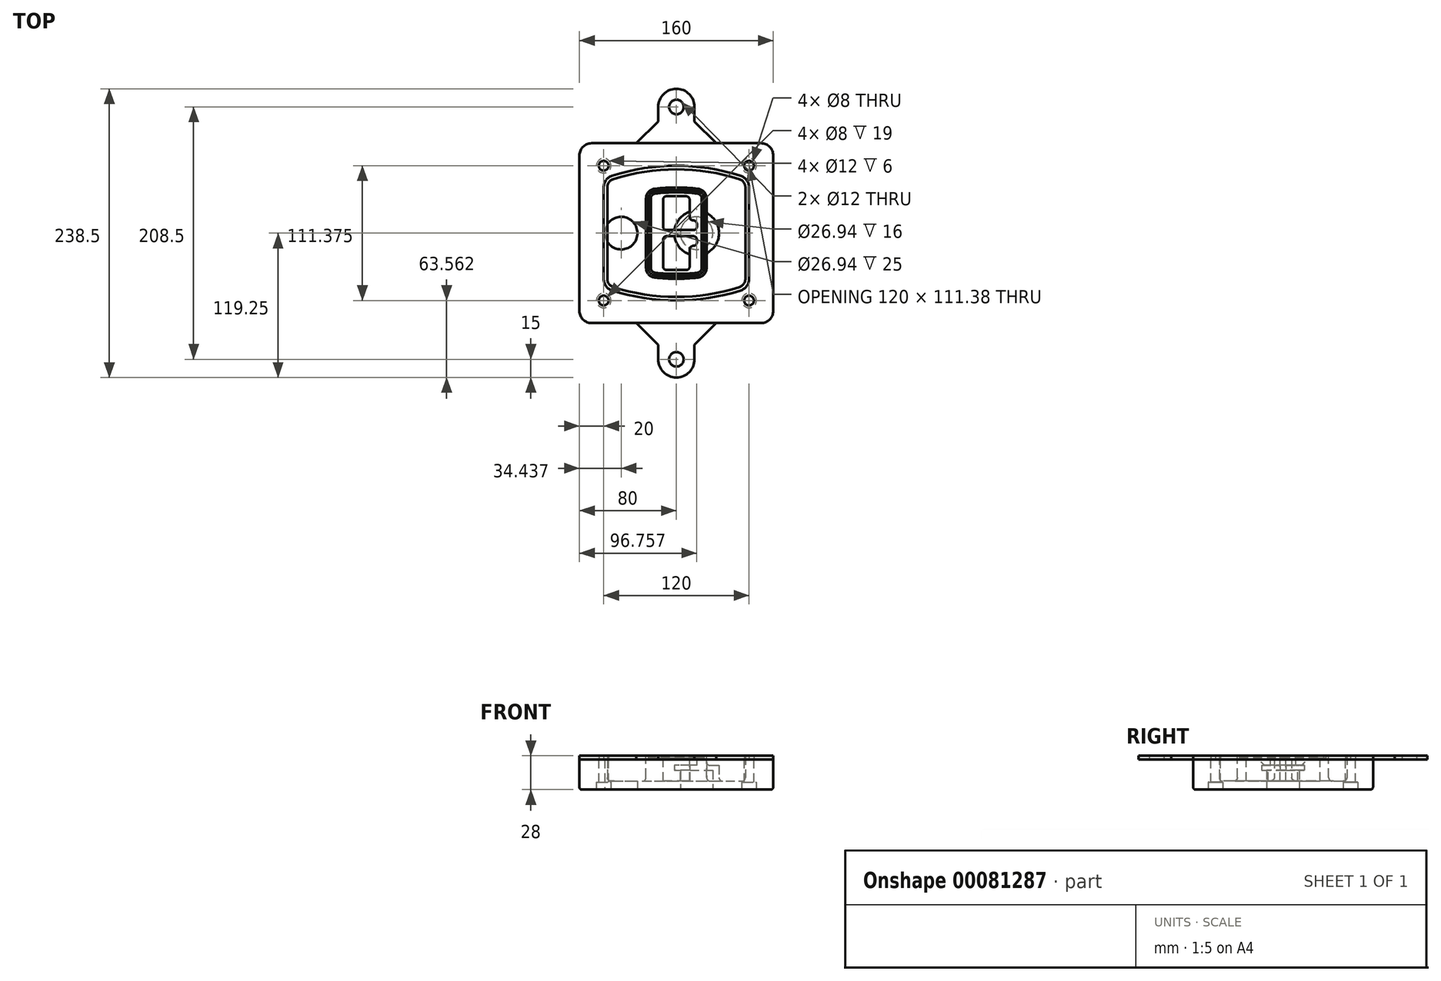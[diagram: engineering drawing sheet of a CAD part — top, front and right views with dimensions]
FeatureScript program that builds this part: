
annotation { "Feature Type Name" : "Feature", "Feature Type Description" : "" }
export const myFeature = defineFeature(function(context is Context, id is Id, definition is map)
    precondition{}
    {
        {
            var Q0;
            Q0=qCreatedBy(makeId("Top.planeOp"),FACE);
            var sketch = newSketch(context, id + "F0", { "sketchPlane" : qUnion([Q0])});
            skPoint(sketch, "E0.rect.middle", {"position": v(0, 0) * mm});
            skLineSegment(sketch, "E1.bottom", {"start": v(-70, -74.25) * mm, "end": v(70, -74.25) * mm});
            skLineSegment(sketch, "E1.top", {"start": v(-70, 74.25) * mm, "end": v(70, 74.25) * mm});
            skLineSegment(sketch, "E1.left", {"start": v(-80, -64.25) * mm, "end": v(-80, 64.25) * mm});
            skLineSegment(sketch, "E1.right", {"start": v(80, -64.25) * mm, "end": v(80, 64.25) * mm});
            skLineSegment(sketch, "E2", {"start": v(-80, 74.25) * mm, "end": v(80, -74.25) * mm, "construction": true});
            skLineSegment(sketch, "E3", {"start": v(80, 74.25) * mm, "end": v(-80, -74.25) * mm, "construction": true});
            skCircle(sketch, "E4", {"center": v(-60, 55.69) * mm, "radius": 4 * mm});
            skCircle(sketch, "E5", {"center": v(60, 55.69) * mm, "radius": 4 * mm});
            skCircle(sketch, "E6", {"center": v(60, -55.69) * mm, "radius": 4 * mm});
            skCircle(sketch, "E7", {"center": v(-60, -55.69) * mm, "radius": 4 * mm});
            skLineSegment(sketch, "E8", {"start": v(-60, 55.69) * mm, "end": v(60, 55.69) * mm, "construction": true});
            skLineSegment(sketch, "E9", {"start": v(60, 55.69) * mm, "end": v(60, -55.69) * mm, "construction": true});
            skLineSegment(sketch, "E10", {"start": v(60, -55.69) * mm, "end": v(-60, -55.69) * mm, "construction": true});
            skLineSegment(sketch, "E11", {"start": v(-60, -55.69) * mm, "end": v(-60, 55.69) * mm, "construction": true});
            skLineSegment(sketch, "E12", {"start": v(-60, 37.87) * mm, "end": v(-60, -37.87) * mm});
            skLineSegment(sketch, "E13", {"start": v(60, 37.87) * mm, "end": v(60, -37.87) * mm});
            skArc(sketch, "E14", {"start": v(53.05, 47.4) * mm, "mid": v(0, 55.69) * mm, "end": v(-53.05, 47.4) * mm});
            skArc(sketch, "E15", {"start": v(-53.05, -47.4) * mm, "mid": v(0, -55.69) * mm, "end": v(53.05, -47.4) * mm});
            skLineSegment(sketch, "E16", {"start": v(-60, 0) * mm, "end": v(60, 0) * mm, "construction": true});
            skPoint(sketch, "E17.visualSharp", {"position": v(-60, -45) * mm});
            skArc(sketch, "E17.filletArc", {"start": v(-60, -37.87) * mm, "mid": v(-58.08, -43.76) * mm, "end": v(-53.05, -47.4) * mm});
            skPoint(sketch, "E18.visualSharp", {"position": v(-60, 45) * mm});
            skArc(sketch, "E18.filletArc", {"start": v(-53.05, 47.4) * mm, "mid": v(-58.08, 43.76) * mm, "end": v(-60, 37.87) * mm});
            skPoint(sketch, "E19.visualSharp", {"position": v(60, 45) * mm});
            skArc(sketch, "E19.filletArc", {"start": v(60, 37.87) * mm, "mid": v(58.08, 43.76) * mm, "end": v(53.05, 47.4) * mm});
            skPoint(sketch, "E20.visualSharp", {"position": v(60, -45) * mm});
            skArc(sketch, "E20.filletArc", {"start": v(53.05, -47.4) * mm, "mid": v(58.08, -43.76) * mm, "end": v(60, -37.87) * mm});
            skPoint(sketch, "E21.visualSharp", {"position": v(-80, 74.25) * mm});
            skArc(sketch, "E21.filletArc", {"start": v(-70, 74.25) * mm, "mid": v(-77.07, 71.32) * mm, "end": v(-80, 64.25) * mm});
            skPoint(sketch, "E22.visualSharp", {"position": v(80, 74.25) * mm});
            skArc(sketch, "E22.filletArc", {"start": v(80, 64.25) * mm, "mid": v(77.07, 71.32) * mm, "end": v(70, 74.25) * mm});
            skPoint(sketch, "E23.visualSharp", {"position": v(80, -74.25) * mm});
            skArc(sketch, "E23.filletArc", {"start": v(70, -74.25) * mm, "mid": v(77.07, -71.32) * mm, "end": v(80, -64.25) * mm});
            skPoint(sketch, "E24.visualSharp", {"position": v(-80, -74.25) * mm});
            skArc(sketch, "E24.filletArc", {"start": v(-80, -64.25) * mm, "mid": v(-77.07, -71.32) * mm, "end": v(-70, -74.25) * mm});
            skArc(sketch, "E25.0", {"start": v(57, 37.87) * mm, "mid": v(55.66, 42) * mm, "end": v(52.14, 44.53) * mm});
            skLineSegment(sketch, "E25.1", {"start": v(57, 37.87) * mm, "end": v(57, -37.87) * mm});
            skArc(sketch, "E25.2", {"start": v(52.14, -44.53) * mm, "mid": v(55.66, -42) * mm, "end": v(57, -37.87) * mm});
            skArc(sketch, "E25.3", {"start": v(-52.14, -44.53) * mm, "mid": v(0, -52.69) * mm, "end": v(52.14, -44.53) * mm});
            skArc(sketch, "E25.4", {"start": v(-57, -37.87) * mm, "mid": v(-55.66, -42) * mm, "end": v(-52.14, -44.53) * mm});
            skArc(sketch, "E25.5", {"start": v(52.14, 44.53) * mm, "mid": v(0, 52.69) * mm, "end": v(-52.14, 44.53) * mm});
            skLineSegment(sketch, "E25.6", {"start": v(-57, 37.87) * mm, "end": v(-57, -37.87) * mm});
            skArc(sketch, "E25.7", {"start": v(-52.14, 44.53) * mm, "mid": v(-55.66, 42) * mm, "end": v(-57, 37.87) * mm});
            skArc(sketch, "E26.0", {"start": v(-54.27, 51.2) * mm, "mid": v(-61.31, 46.12) * mm, "end": v(-64, 37.87) * mm});
            skArc(sketch, "E26.1", {"start": v(54.27, 51.2) * mm, "mid": v(0, 59.69) * mm, "end": v(-54.27, 51.2) * mm});
            skArc(sketch, "E26.2", {"start": v(64, 37.87) * mm, "mid": v(61.31, 46.12) * mm, "end": v(54.27, 51.2) * mm});
            skLineSegment(sketch, "E26.3", {"start": v(64, 37.87) * mm, "end": v(64, -37.87) * mm});
            skArc(sketch, "E26.4", {"start": v(54.27, -51.2) * mm, "mid": v(61.31, -46.12) * mm, "end": v(64, -37.87) * mm});
            skLineSegment(sketch, "E26.5", {"start": v(-64, 37.87) * mm, "end": v(-64, -37.87) * mm});
            skArc(sketch, "E26.6", {"start": v(-54.27, -51.2) * mm, "mid": v(0, -59.69) * mm, "end": v(54.27, -51.2) * mm});
            skArc(sketch, "E26.7", {"start": v(-64, -37.87) * mm, "mid": v(-61.31, -46.12) * mm, "end": v(-54.27, -51.2) * mm});
            skSolve(sketch);
        }
        {
            var Q0;
            Q0=makeQuery(id+"F0.imprint","IMPRINT",FACE,{"disambiguationData":[TD([[makeQuery(id+"F0.imprint","IMPRINT",EDGE,{"derivedFrom":sQuery(id+"F0.wireOp",EDGE,"E1.bottom")}),1.0]])]});
            var Q1;
            Q1=makeQuery(id+"F0.imprint","IMPRINT",FACE,{"disambiguationData":[TD([[makeQuery(id+"F0.imprint","IMPRINT",EDGE,{"derivedFrom":sQuery(id+"F0.wireOp",EDGE,"E12")}),1.0]])]});
            var Q2;
            Q2=makeQuery(id+"F0.imprint","IMPRINT",FACE,{"disambiguationData":[TD([[makeQuery(id+"F0.imprint","IMPRINT",EDGE,{"derivedFrom":sQuery(id+"F0.wireOp",EDGE,"E25.0")}),1.0]])]});
            var Q3;
            Q3=makeQuery(id+"F0.imprint","IMPRINT",FACE,{"disambiguationData":[TD([[makeQuery(id+"F0.imprint","IMPRINT",EDGE,{"derivedFrom":sQuery(id+"F0.wireOp",EDGE,"E12")}),-1.0]])]});
            extrude(context, id + "F1", {"entities" : qUnion([Q0, Q1, Q2, Q3]), "oppositeDirection" : true, "depth" : 25 * mm});
        }
        {
            var Q0;
            Q0=makeQuery(id+"F0.imprint","IMPRINT",FACE,{"disambiguationData":[TD([[makeQuery(id+"F0.imprint","IMPRINT",EDGE,{"derivedFrom":sQuery(id+"F0.wireOp",EDGE,"E12")}),1.0]])]});
            extrude(context, id + "F2", {"entities" : qUnion([Q0]), "operationType" : NewBodyOperationType.ADD, "depth" : 3 * mm});
        }
        {
            var Q0;
            Q0=makeQuery(id+"F0.imprint","IMPRINT",FACE,{"disambiguationData":[TD([[makeQuery(id+"F0.imprint","IMPRINT",EDGE,{"derivedFrom":sQuery(id+"F0.wireOp",EDGE,"E25.0")}),1.0]])]});
            extrude(context, id + "F3", {"entities" : qUnion([Q0]), "operationType" : NewBodyOperationType.REMOVE, "oppositeDirection" : true, "depth" : 18 * mm});
        }
        {
            var Q0;
            Q0=makeQuery(id+"F2.opExtrude","CAP_FACE",FACE,{"disambiguationData":[OSD([sQuery(id+"F0.wireOp",EDGE,"E12"),sQuery(id+"F0.wireOp",EDGE,"E13"),sQuery(id+"F0.wireOp",EDGE,"E14"),sQuery(id+"F0.wireOp",EDGE,"E15"),sQuery(id+"F0.wireOp",EDGE,"E17.filletArc"),sQuery(id+"F0.wireOp",EDGE,"E18.filletArc"),sQuery(id+"F0.wireOp",EDGE,"E19.filletArc"),sQuery(id+"F0.wireOp",EDGE,"E20.filletArc"),sQuery(id+"F0.wireOp",EDGE,"E25.0"),sQuery(id+"F0.wireOp",EDGE,"E25.1"),sQuery(id+"F0.wireOp",EDGE,"E25.2"),sQuery(id+"F0.wireOp",EDGE,"E25.3"),sQuery(id+"F0.wireOp",EDGE,"E25.4"),sQuery(id+"F0.wireOp",EDGE,"E25.5"),sQuery(id+"F0.wireOp",EDGE,"E25.6"),sQuery(id+"F0.wireOp",EDGE,"E25.7")])],"isStart":false});
            var sketch = newSketch(context, id + "F4", { "sketchPlane" : qUnion([Q0])});
            skArc(sketch, "E27.0", {"start": v(-17.92, -36.65) * mm, "mid": v(0, -37.69) * mm, "end": v(17.92, -36.65) * mm});
            skArc(sketch, "E28.0", {"start": v(17.92, 36.65) * mm, "mid": v(0, 37.69) * mm, "end": v(-17.92, 36.65) * mm});
            skLineSegment(sketch, "E29", {"start": v(-25, 28.7) * mm, "end": v(-25, -28.7) * mm});
            skLineSegment(sketch, "E30", {"start": v(25, 28.7) * mm, "end": v(25, -28.7) * mm});
            skLineSegment(sketch, "E31", {"start": v(-25, 35.67) * mm, "end": v(25, 35.67) * mm, "construction": true});
            skLineSegment(sketch, "E32", {"start": v(-25, -35.67) * mm, "end": v(25, -35.67) * mm, "construction": true});
            skPoint(sketch, "E33.visualSharp", {"position": v(-25, 35.67) * mm});
            skArc(sketch, "E33.filletArc", {"start": v(-17.92, 36.65) * mm, "mid": v(-22.97, 34.03) * mm, "end": v(-25, 28.7) * mm});
            skPoint(sketch, "E34.visualSharp", {"position": v(25, 35.67) * mm});
            skArc(sketch, "E34.filletArc", {"start": v(25, 28.7) * mm, "mid": v(22.97, 34.03) * mm, "end": v(17.92, 36.65) * mm});
            skPoint(sketch, "E35.visualSharp", {"position": v(25, -35.67) * mm});
            skArc(sketch, "E35.filletArc", {"start": v(17.92, -36.65) * mm, "mid": v(22.97, -34.03) * mm, "end": v(25, -28.7) * mm});
            skPoint(sketch, "E36.visualSharp", {"position": v(-25, -35.67) * mm});
            skArc(sketch, "E36.filletArc", {"start": v(-25, -28.7) * mm, "mid": v(-22.97, -34.03) * mm, "end": v(-17.92, -36.65) * mm});
            skArc(sketch, "E37.0", {"start": v(52.14, 44.53) * mm, "mid": v(0, 52.69) * mm, "end": v(-52.14, 44.53) * mm});
            skArc(sketch, "E37.1", {"start": v(-52.14, 44.53) * mm, "mid": v(-55.66, 42) * mm, "end": v(-57, 37.87) * mm});
            skLineSegment(sketch, "E37.2", {"start": v(-57, 37.87) * mm, "end": v(-57, -37.87) * mm});
            skArc(sketch, "E37.3", {"start": v(-57, -37.87) * mm, "mid": v(-55.66, -42) * mm, "end": v(-52.14, -44.53) * mm});
            skArc(sketch, "E37.4", {"start": v(-52.14, -44.53) * mm, "mid": v(0, -52.69) * mm, "end": v(52.14, -44.53) * mm});
            skArc(sketch, "E37.5", {"start": v(52.14, -44.53) * mm, "mid": v(55.66, -42) * mm, "end": v(57, -37.87) * mm});
            skLineSegment(sketch, "E37.6", {"start": v(57, 37.87) * mm, "end": v(57, -37.87) * mm});
            skArc(sketch, "E37.7", {"start": v(57, 37.87) * mm, "mid": v(55.66, 42) * mm, "end": v(52.14, 44.53) * mm});
            skLineSegment(sketch, "E38.0", {"start": v(23, 28.7) * mm, "end": v(23, -28.7) * mm});
            skArc(sketch, "E38.1", {"start": v(17.7, -34.67) * mm, "mid": v(21.48, -32.7) * mm, "end": v(23, -28.7) * mm});
            skArc(sketch, "E38.2", {"start": v(-17.7, -34.67) * mm, "mid": v(0, -35.69) * mm, "end": v(17.7, -34.67) * mm});
            skArc(sketch, "E38.3", {"start": v(-23, -28.7) * mm, "mid": v(-21.48, -32.7) * mm, "end": v(-17.7, -34.67) * mm});
            skLineSegment(sketch, "E38.4", {"start": v(-23, 28.7) * mm, "end": v(-23, -28.7) * mm});
            skArc(sketch, "E38.5", {"start": v(23, 28.7) * mm, "mid": v(21.48, 32.7) * mm, "end": v(17.7, 34.67) * mm});
            skArc(sketch, "E38.6", {"start": v(-17.7, 34.67) * mm, "mid": v(-21.48, 32.7) * mm, "end": v(-23, 28.7) * mm});
            skArc(sketch, "E38.7", {"start": v(17.7, 34.67) * mm, "mid": v(0, 35.69) * mm, "end": v(-17.7, 34.67) * mm});
            skArc(sketch, "E39.0", {"start": v(21, 28.7) * mm, "mid": v(19.99, 31.37) * mm, "end": v(17.46, 32.68) * mm});
            skLineSegment(sketch, "E39.1", {"start": v(21, 28.7) * mm, "end": v(21, -28.7) * mm});
            skArc(sketch, "E39.2", {"start": v(17.46, -32.68) * mm, "mid": v(19.99, -31.37) * mm, "end": v(21, -28.7) * mm});
            skArc(sketch, "E39.3", {"start": v(-17.46, -32.68) * mm, "mid": v(0, -33.69) * mm, "end": v(17.46, -32.68) * mm});
            skArc(sketch, "E39.4", {"start": v(-21, -28.7) * mm, "mid": v(-19.99, -31.37) * mm, "end": v(-17.46, -32.68) * mm});
            skArc(sketch, "E39.5", {"start": v(17.46, 32.68) * mm, "mid": v(0, 33.69) * mm, "end": v(-17.46, 32.68) * mm});
            skLineSegment(sketch, "E39.6", {"start": v(-21, 28.7) * mm, "end": v(-21, -28.7) * mm});
            skArc(sketch, "E39.7", {"start": v(-17.46, 32.68) * mm, "mid": v(-19.99, 31.37) * mm, "end": v(-21, 28.7) * mm});
            skLineSegment(sketch, "E40", {"start": v(-25, 0) * mm, "end": v(25, 0) * mm, "construction": true});
            skLineSegment(sketch, "E41", {"start": v(-11, 5.5) * mm, "end": v(-11, 27.5) * mm});
            skLineSegment(sketch, "E42", {"start": v(-8, 30.5) * mm, "end": v(8, 30.5) * mm});
            skLineSegment(sketch, "E43", {"start": v(11, 27.5) * mm, "end": v(11, 13.5) * mm});
            skLineSegment(sketch, "E44", {"start": v(14, 10.5) * mm, "end": v(14, 10.5) * mm});
            skLineSegment(sketch, "E45", {"start": v(17, 7.5) * mm, "end": v(17, 5.5) * mm});
            skLineSegment(sketch, "E46", {"start": v(14, 2.5) * mm, "end": v(-8, 2.5) * mm});
            skPoint(sketch, "E47.visualSharp", {"position": v(-11, 30.5) * mm});
            skArc(sketch, "E47.filletArc", {"start": v(-8, 30.5) * mm, "mid": v(-10.12, 29.62) * mm, "end": v(-11, 27.5) * mm});
            skPoint(sketch, "E48.visualSharp", {"position": v(11, 30.5) * mm});
            skArc(sketch, "E48.filletArc", {"start": v(11, 27.5) * mm, "mid": v(10.12, 29.62) * mm, "end": v(8, 30.5) * mm});
            skPoint(sketch, "E49.visualSharp", {"position": v(11, 10.5) * mm});
            skArc(sketch, "E49.filletArc", {"start": v(11, 13.5) * mm, "mid": v(11.88, 11.38) * mm, "end": v(14, 10.5) * mm});
            skPoint(sketch, "E50.visualSharp", {"position": v(17, 10.5) * mm});
            skArc(sketch, "E50.filletArc", {"start": v(17, 7.5) * mm, "mid": v(16.12, 9.62) * mm, "end": v(14, 10.5) * mm});
            skPoint(sketch, "E51.visualSharp", {"position": v(17, 2.5) * mm});
            skArc(sketch, "E51.filletArc", {"start": v(14, 2.5) * mm, "mid": v(16.12, 3.38) * mm, "end": v(17, 5.5) * mm});
            skPoint(sketch, "E52.visualSharp", {"position": v(-11, 2.5) * mm});
            skArc(sketch, "E52.filletArc", {"start": v(-11, 5.5) * mm, "mid": v(-10.12, 3.38) * mm, "end": v(-8, 2.5) * mm});
            skLineSegment(sketch, "E53.0.MirrorCS", {"start": v(14, -2.5) * mm, "end": v(-8, -2.5) * mm});
            skArc(sketch, "E54.0.MirrorCS", {"start": v(-11, -5.5) * mm, "mid": v(-10.12, -3.38) * mm, "end": v(-8, -2.5) * mm});
            skLineSegment(sketch, "E55.0.MirrorCS", {"start": v(-11, -5.5) * mm, "end": v(-11, -27.5) * mm});
            skArc(sketch, "E56.0.MirrorCS", {"start": v(-8, -30.5) * mm, "mid": v(-10.12, -29.62) * mm, "end": v(-11, -27.5) * mm});
            skLineSegment(sketch, "E57.0.MirrorCS", {"start": v(-8, -30.5) * mm, "end": v(8, -30.5) * mm});
            skArc(sketch, "E58.0.MirrorCS", {"start": v(11, -27.5) * mm, "mid": v(10.12, -29.62) * mm, "end": v(8, -30.5) * mm});
            skLineSegment(sketch, "E59.0.MirrorCS", {"start": v(11, -27.5) * mm, "end": v(11, -13.5) * mm});
            skArc(sketch, "E60.0.MirrorCS", {"start": v(11, -13.5) * mm, "mid": v(11.88, -11.38) * mm, "end": v(14, -10.5) * mm});
            skArc(sketch, "E61.0.MirrorCS", {"start": v(17, -7.5) * mm, "mid": v(16.12, -9.62) * mm, "end": v(14, -10.5) * mm});
            skLineSegment(sketch, "E62.0.MirrorCS", {"start": v(17, -7.5) * mm, "end": v(17, -5.5) * mm});
            skArc(sketch, "E63.0.MirrorCS", {"start": v(14, -2.5) * mm, "mid": v(16.12, -3.38) * mm, "end": v(17, -5.5) * mm});
            skSolve(sketch);
        }
        {
            var Q0;
            Q0=makeQuery(id+"F4.imprint","IMPRINT",FACE,{"disambiguationData":[TD([[makeQuery(id+"F4.imprint","IMPRINT",EDGE,{"derivedFrom":sQuery(id+"F4.wireOp",EDGE,"E27.0")}),1.0]])]});
            var Q1;
            Q1=makeQuery(id+"F4.imprint","IMPRINT",FACE,{"disambiguationData":[TD([[makeQuery(id+"F4.imprint","IMPRINT",EDGE,{"derivedFrom":sQuery(id+"F4.wireOp",EDGE,"E38.0")}),-1.0]])]});
            var Q2;
            Q2=makeQuery(id+"F4.imprint","IMPRINT",FACE,{"disambiguationData":[TD([[makeQuery(id+"F4.imprint","IMPRINT",EDGE,{"derivedFrom":sQuery(id+"F4.wireOp",EDGE,"E39.0")}),1.0]])]});
            extrude(context, id + "F5", {"entities" : qUnion([Q0, Q1, Q2]), "operationType" : NewBodyOperationType.ADD, "endBound" : BoundingType.UP_TO_NEXT, "oppositeDirection" : true, "depth" : 25 * mm});
        }
        {
            var Q0;
            Q0=makeQuery(id+"F4.imprint","IMPRINT",FACE,{"disambiguationData":[TD([[makeQuery(id+"F4.imprint","IMPRINT",EDGE,{"derivedFrom":sQuery(id+"F4.wireOp",EDGE,"E38.0")}),-1.0]])]});
            extrude(context, id + "F6", {"entities" : qUnion([Q0]), "operationType" : NewBodyOperationType.REMOVE, "oppositeDirection" : true, "depth" : 2 * mm});
        }
        {
            var Q0;
            Q0=makeQuery(id+"F1.opExtrude","CAP_FACE",FACE,{"disambiguationData":[OSD([sQuery(id+"F0.wireOp",EDGE,"E1.bottom"),sQuery(id+"F0.wireOp",EDGE,"E1.top"),sQuery(id+"F0.wireOp",EDGE,"E1.left"),sQuery(id+"F0.wireOp",EDGE,"E1.right"),sQuery(id+"F0.wireOp",EDGE,"E4"),sQuery(id+"F0.wireOp",EDGE,"E5"),sQuery(id+"F0.wireOp",EDGE,"E6"),sQuery(id+"F0.wireOp",EDGE,"E7"),sQuery(id+"F0.wireOp",EDGE,"E21.filletArc"),sQuery(id+"F0.wireOp",EDGE,"E22.filletArc"),sQuery(id+"F0.wireOp",EDGE,"E23.filletArc"),sQuery(id+"F0.wireOp",EDGE,"E24.filletArc")])],"isStart":false});
            var sketch = newSketch(context, id + "F7", { "sketchPlane" : qUnion([Q0])});
            skCircle(sketch, "E64", {"center": v(16.76, 0) * mm, "radius": 13.47 * mm});
            skCircle(sketch, "E65", {"center": v(-45.56, 0) * mm, "radius": 13.47 * mm});
            skLineSegment(sketch, "E66", {"start": v(80, 0) * mm, "end": v(-80, 0) * mm});
            skCircle(sketch, "E67", {"center": v(16.76, 0) * mm, "radius": 18.47 * mm});
            skCircle(sketch, "E68", {"center": v(60, -55.69) * mm, "radius": 6 * mm});
            skCircle(sketch, "E69", {"center": v(-60, -55.69) * mm, "radius": 6 * mm});
            skCircle(sketch, "E70", {"center": v(-60, 55.69) * mm, "radius": 6 * mm});
            skCircle(sketch, "E71", {"center": v(60, 55.69) * mm, "radius": 6 * mm});
            skSolve(sketch);
        }
        {
            var Q0;
            {var subQ1=sQuery(id+"F7.wireOp",EDGE,"E66");var subQ4=sQuery(id+"F7.wireOp",EDGE,"E64");var subQ6=makeQuery(id+"F7.imprint","INTERSECT",VERTEX,{"disambiguationData":[OD(0.0)],"derivedFrom":[subQ4,subQ1]});Q0=makeQuery(id+"F7.imprint","IMPRINT",FACE,{"disambiguationData":[TD([[makeQuery(id+"F7.imprint","IMPRINT",EDGE,{"disambiguationData":[TD([[subQ6,-1.0]])],"derivedFrom":subQ4}),-1.0]])]});}
            var Q1;
            {var subQ0=sQuery(id+"F7.wireOp",EDGE,"E66");var subQ1=sQuery(id+"F7.wireOp",EDGE,"E64");var subQ3=makeQuery(id+"F7.imprint","INTERSECT",VERTEX,{"disambiguationData":[OD(0.0)],"derivedFrom":[subQ1,subQ0]});Q1=makeQuery(id+"F7.imprint","IMPRINT",FACE,{"disambiguationData":[TD([[makeQuery(id+"F7.imprint","IMPRINT",EDGE,{"disambiguationData":[TD([[subQ3,-1.0]])],"derivedFrom":subQ1}),1.0]])]});}
            var Q2;
            {var subQ0=sQuery(id+"F7.wireOp",EDGE,"E66");var subQ1=sQuery(id+"F7.wireOp",EDGE,"E64");var subQ3=makeQuery(id+"F7.imprint","INTERSECT",VERTEX,{"disambiguationData":[OD(0.0)],"derivedFrom":[subQ1,subQ0]});Q2=makeQuery(id+"F7.imprint","IMPRINT",FACE,{"disambiguationData":[TD([[makeQuery(id+"F7.imprint","IMPRINT",EDGE,{"disambiguationData":[TD([[subQ3,1.0]])],"derivedFrom":subQ1}),1.0]])]});}
            var Q3;
            {var subQ1=sQuery(id+"F7.wireOp",EDGE,"E66");var subQ4=sQuery(id+"F7.wireOp",EDGE,"E64");var subQ6=makeQuery(id+"F7.imprint","INTERSECT",VERTEX,{"disambiguationData":[OD(0.0)],"derivedFrom":[subQ4,subQ1]});Q3=makeQuery(id+"F7.imprint","IMPRINT",FACE,{"disambiguationData":[TD([[makeQuery(id+"F7.imprint","IMPRINT",EDGE,{"disambiguationData":[TD([[subQ6,1.0]])],"derivedFrom":subQ4}),-1.0]])]});}
            extrude(context, id + "F8", {"entities" : qUnion([Q0, Q1, Q2, Q3]), "operationType" : NewBodyOperationType.ADD, "oppositeDirection" : true, "depth" : 20 * mm});
        }
        {
            var Q0;
            {var subQ0=sQuery(id+"F7.wireOp",EDGE,"E66");var subQ1=sQuery(id+"F7.wireOp",EDGE,"E64");var subQ3=makeQuery(id+"F7.imprint","INTERSECT",VERTEX,{"disambiguationData":[OD(0.0)],"derivedFrom":[subQ1,subQ0]});Q0=makeQuery(id+"F7.imprint","IMPRINT",FACE,{"disambiguationData":[TD([[makeQuery(id+"F7.imprint","IMPRINT",EDGE,{"disambiguationData":[TD([[subQ3,-1.0]])],"derivedFrom":subQ1}),1.0]])]});}
            var Q1;
            {var subQ0=sQuery(id+"F7.wireOp",EDGE,"E66");var subQ1=sQuery(id+"F7.wireOp",EDGE,"E64");var subQ3=makeQuery(id+"F7.imprint","INTERSECT",VERTEX,{"disambiguationData":[OD(0.0)],"derivedFrom":[subQ1,subQ0]});Q1=makeQuery(id+"F7.imprint","IMPRINT",FACE,{"disambiguationData":[TD([[makeQuery(id+"F7.imprint","IMPRINT",EDGE,{"disambiguationData":[TD([[subQ3,1.0]])],"derivedFrom":subQ1}),1.0]])]});}
            extrude(context, id + "F9", {"entities" : qUnion([Q0, Q1]), "operationType" : NewBodyOperationType.REMOVE, "oppositeDirection" : true, "depth" : 16 * mm});
        }
        {
            var Q0;
            {var subQ0=sQuery(id+"F7.wireOp",EDGE,"E66");var subQ1=sQuery(id+"F7.wireOp",EDGE,"E65");var subQ3=makeQuery(id+"F7.imprint","INTERSECT",VERTEX,{"disambiguationData":[OD(0.0)],"derivedFrom":[subQ1,subQ0]});Q0=makeQuery(id+"F7.imprint","IMPRINT",FACE,{"disambiguationData":[TD([[makeQuery(id+"F7.imprint","IMPRINT",EDGE,{"disambiguationData":[TD([[subQ3,-1.0]])],"derivedFrom":subQ1}),1.0]])]});}
            var Q1;
            {var subQ0=sQuery(id+"F7.wireOp",EDGE,"E66");var subQ1=sQuery(id+"F7.wireOp",EDGE,"E65");var subQ3=makeQuery(id+"F7.imprint","INTERSECT",VERTEX,{"disambiguationData":[OD(0.0)],"derivedFrom":[subQ1,subQ0]});Q1=makeQuery(id+"F7.imprint","IMPRINT",FACE,{"disambiguationData":[TD([[makeQuery(id+"F7.imprint","IMPRINT",EDGE,{"disambiguationData":[TD([[subQ3,1.0]])],"derivedFrom":subQ1}),1.0]])]});}
            extrude(context, id + "F10", {"entities" : qUnion([Q0, Q1]), "operationType" : NewBodyOperationType.REMOVE, "oppositeDirection" : true, "depth" : 25 * mm});
        }
        {
            var Q0;
            Q0=makeQuery(id+"F7.imprint","IMPRINT",FACE,{"disambiguationData":[TD([[makeQuery(id+"F7.imprint","IMPRINT",EDGE,{"derivedFrom":sQuery(id+"F7.wireOp",EDGE,"E68")}),1.0]])]});
            var Q1;
            Q1=makeQuery(id+"F7.imprint","IMPRINT",FACE,{"disambiguationData":[TD([[makeQuery(id+"F7.imprint","IMPRINT",EDGE,{"derivedFrom":makeQuery(id+"F1.opExtrude","CAP_EDGE",EDGE,{"disambiguationData":[OSD([sQuery(id+"F0.wireOp",EDGE,"E5")])],"isStart":false})}),-1.0]])]});
            var Q2;
            Q2=makeQuery(id+"F7.imprint","IMPRINT",FACE,{"disambiguationData":[TD([[makeQuery(id+"F7.imprint","IMPRINT",EDGE,{"derivedFrom":sQuery(id+"F7.wireOp",EDGE,"E69")}),1.0]])]});
            var Q3;
            Q3=makeQuery(id+"F7.imprint","IMPRINT",FACE,{"disambiguationData":[TD([[makeQuery(id+"F7.imprint","IMPRINT",EDGE,{"derivedFrom":makeQuery(id+"F1.opExtrude","CAP_EDGE",EDGE,{"disambiguationData":[OSD([sQuery(id+"F0.wireOp",EDGE,"E4")])],"isStart":false})}),-1.0]])]});
            var Q4;
            Q4=makeQuery(id+"F7.imprint","IMPRINT",FACE,{"disambiguationData":[TD([[makeQuery(id+"F7.imprint","IMPRINT",EDGE,{"derivedFrom":sQuery(id+"F7.wireOp",EDGE,"E70")}),1.0]])]});
            var Q5;
            Q5=makeQuery(id+"F7.imprint","IMPRINT",FACE,{"disambiguationData":[TD([[makeQuery(id+"F7.imprint","IMPRINT",EDGE,{"derivedFrom":makeQuery(id+"F1.opExtrude","CAP_EDGE",EDGE,{"disambiguationData":[OSD([sQuery(id+"F0.wireOp",EDGE,"E7")])],"isStart":false})}),-1.0]])]});
            var Q6;
            Q6=makeQuery(id+"F7.imprint","IMPRINT",FACE,{"disambiguationData":[TD([[makeQuery(id+"F7.imprint","IMPRINT",EDGE,{"derivedFrom":sQuery(id+"F7.wireOp",EDGE,"E71")}),1.0]])]});
            var Q7;
            Q7=makeQuery(id+"F7.imprint","IMPRINT",FACE,{"disambiguationData":[TD([[makeQuery(id+"F7.imprint","IMPRINT",EDGE,{"derivedFrom":makeQuery(id+"F1.opExtrude","CAP_EDGE",EDGE,{"disambiguationData":[OSD([sQuery(id+"F0.wireOp",EDGE,"E6")])],"isStart":false})}),-1.0]])]});
            extrude(context, id + "F11", {"entities" : qUnion([Q0, Q1, Q2, Q3, Q4, Q5, Q6, Q7]), "operationType" : NewBodyOperationType.REMOVE, "oppositeDirection" : true, "depth" : 6 * mm});
        }
        {
            var Q0;
            Q0=makeQuery(id+"F9.boolean.opBoolean","COPY",FACE,{"derivedFrom":makeQuery(id+"F9.opExtrude","CAP_FACE",FACE,{"disambiguationData":[OSD([sQuery(id+"F7.wireOp",EDGE,"E64")])],"isStart":false})});
            var sketch = newSketch(context, id + "F12", { "sketchPlane" : qUnion([Q0])});
            skArc(sketch, "E72.0", {"start": v(11, 17.55) * mm, "mid": v(2.57, 11.82) * mm, "end": v(-1.54, 2.5) * mm});
            skArc(sketch, "E72.1", {"start": v(-1.54, -2.5) * mm, "mid": v(2.57, -11.82) * mm, "end": v(11, -17.55) * mm});
            skLineSegment(sketch, "E73", {"start": v(-1.54, -2.5) * mm, "end": v(14, -2.5) * mm});
            skLineSegment(sketch, "E74.0", {"start": v(14, 2.5) * mm, "end": v(-1.54, 2.5) * mm});
            skArc(sketch, "E74.1", {"start": v(14, 2.5) * mm, "mid": v(16.12, 3.38) * mm, "end": v(17, 5.5) * mm});
            skLineSegment(sketch, "E74.2", {"start": v(17, 7.5) * mm, "end": v(17, 5.5) * mm});
            skArc(sketch, "E74.3", {"start": v(17, 7.5) * mm, "mid": v(16.12, 9.62) * mm, "end": v(14, 10.5) * mm});
            skArc(sketch, "E74.4", {"start": v(11, 13.5) * mm, "mid": v(11.88, 11.38) * mm, "end": v(14, 10.5) * mm});
            skLineSegment(sketch, "E74.5", {"start": v(11, 17.55) * mm, "end": v(11, 13.5) * mm});
            skLineSegment(sketch, "E74.7", {"start": v(14, -2.5) * mm, "end": v(-1.54, -2.5) * mm});
            skArc(sketch, "E74.8", {"start": v(14, -2.5) * mm, "mid": v(16.12, -3.38) * mm, "end": v(17, -5.5) * mm});
            skLineSegment(sketch, "E74.9", {"start": v(17, -7.5) * mm, "end": v(17, -5.5) * mm});
            skArc(sketch, "E74.10", {"start": v(17, -7.5) * mm, "mid": v(16.12, -9.62) * mm, "end": v(14, -10.5) * mm});
            skArc(sketch, "E74.11", {"start": v(11, -13.5) * mm, "mid": v(11.88, -11.38) * mm, "end": v(14, -10.5) * mm});
            skLineSegment(sketch, "E74.12", {"start": v(11, -17.55) * mm, "end": v(11, -13.5) * mm});
            skPoint(sketch, "E75.orphan", {"position": v(11, -27.5) * mm});
            skPoint(sketch, "E76.orphan", {"position": v(-8, -2.5) * mm});
            skPoint(sketch, "E77.orphan", {"position": v(-8, 2.5) * mm});
            skPoint(sketch, "E78.orphan", {"position": v(11, 27.5) * mm});
            skSolve(sketch);
        }
        {
            var Q0;
            {var subQ7=sQuery(id+"F12.wireOp",EDGE,"E72.0");var subQ14=sQuery(id+"F12.wireOp",EDGE,"E72.1");var subQ16=sQuery(id+"F12.wireOp",EDGE,"E74.1");var subQ18=sQuery(id+"F12.wireOp",EDGE,"E74.8");Q0=qUnion([makeQuery(id+"F12.imprint","IMPRINT",FACE,{"disambiguationData":[TD([[makeQuery(id+"F12.imprint","IMPRINT",EDGE,{"derivedFrom":subQ7}),1.0]])]}),makeQuery(id+"F12.imprint","IMPRINT",FACE,{"disambiguationData":[TD([[makeQuery(id+"F12.imprint","IMPRINT",EDGE,{"derivedFrom":subQ14}),1.0]])]}),makeQuery(id+"F12.imprint","IMPRINT",FACE,{"disambiguationData":[TD([[makeQuery(id+"F12.imprint","IMPRINT",EDGE,{"derivedFrom":subQ16}),1.0]])]}),makeQuery(id+"F12.imprint","IMPRINT",FACE,{"disambiguationData":[TD([[makeQuery(id+"F12.imprint","IMPRINT",EDGE,{"derivedFrom":subQ18}),-1.0]])]})]);}
            var Q1;
            Q1=makeQuery(id+"F5.boolean.opBoolean","SPLIT",FACE,{"disambiguationData":[TD([makeQuery(id+"F5.opExtrude","SWEPT_FACE",FACE,{"disambiguationData":[OSD([sQuery(id+"F4.wireOp",EDGE,"E41")])]})])],"derivedFrom":makeQuery(id+"F3.boolean.opBoolean","COPY",FACE,{"derivedFrom":makeQuery(id+"F3.opExtrude","CAP_FACE",FACE,{"disambiguationData":[OSD([sQuery(id+"F0.wireOp",EDGE,"E25.0"),sQuery(id+"F0.wireOp",EDGE,"E25.1"),sQuery(id+"F0.wireOp",EDGE,"E25.2"),sQuery(id+"F0.wireOp",EDGE,"E25.3"),sQuery(id+"F0.wireOp",EDGE,"E25.4"),sQuery(id+"F0.wireOp",EDGE,"E25.5"),sQuery(id+"F0.wireOp",EDGE,"E25.6"),sQuery(id+"F0.wireOp",EDGE,"E25.7")])],"isStart":false})})});
            extrude(context, id + "F13", {"entities" : qUnion([Q0]), "operationType" : NewBodyOperationType.REMOVE, "endBound" : BoundingType.UP_TO_SURFACE, "endBoundEntityFace" : qUnion([Q1]), "depth" : 25 * mm});
        }
        {
            var Q0;
            Q0=makeQuery(id+"F3.boolean.opBoolean","COPY",EDGE,{"derivedFrom":makeQuery(id+"F3.opExtrude","CAP_EDGE",EDGE,{"disambiguationData":[OSD([sQuery(id+"F0.wireOp",EDGE,"E25.6")])],"isStart":false})});
            var Q1;
            Q1=makeQuery(id+"F8.boolean.opBoolean","INTERSECT",EDGE,{"derivedFrom":[makeQuery(id+"F5.opExtrude","SWEPT_FACE",FACE,{"disambiguationData":[OSD([sQuery(id+"F4.wireOp",EDGE,"E30")])]}),makeQuery(id+"F8.opExtrude","CAP_FACE",FACE,{"disambiguationData":[OSD([sQuery(id+"F7.wireOp",EDGE,"E67")])],"isStart":false})]});
            var Q2;
            Q2=makeQuery(id+"F8.boolean.opBoolean","INTERSECT",EDGE,{"disambiguationData":[OD(1.0)],"derivedFrom":[makeQuery(id+"F5.opExtrude","SWEPT_FACE",FACE,{"disambiguationData":[OSD([sQuery(id+"F4.wireOp",EDGE,"E30")])]}),makeQuery(id+"F8.opExtrude","SWEPT_FACE",FACE,{"disambiguationData":[OSD([sQuery(id+"F7.wireOp",EDGE,"E67")])]})]});
            var Q3;
            {var subQ0=sQuery(id+"F4.wireOp",EDGE,"E30");Q3=makeQuery(id+"F8.boolean.opBoolean","SPLIT",EDGE,{"disambiguationData":[TD([makeQuery(id+"F5.opExtrude","SWEPT_FACE",FACE,{"disambiguationData":[OSD([sQuery(id+"F4.wireOp",EDGE,"E35.filletArc")])]})])],"derivedFrom":makeQuery(id+"F5.opExtrude","CAP_EDGE",EDGE,{"disambiguationData":[OSD([subQ0])],"isStart":false})});}
            var Q4;
            {var subQ0=sQuery(id+"F0.wireOp",EDGE,"E25.7");var subQ1=sQuery(id+"F0.wireOp",EDGE,"E25.1");var subQ2=sQuery(id+"F0.wireOp",EDGE,"E25.6");var subQ3=sQuery(id+"F0.wireOp",EDGE,"E25.5");var subQ4=sQuery(id+"F0.wireOp",EDGE,"E25.4");var subQ5=sQuery(id+"F0.wireOp",EDGE,"E25.0");var subQ6=sQuery(id+"F0.wireOp",EDGE,"E25.2");var subQ7=sQuery(id+"F0.wireOp",EDGE,"E25.3");Q4=makeQuery(id+"F8.boolean.opBoolean","INTERSECT",EDGE,{"derivedFrom":[makeQuery(id+"F5.boolean.opBoolean","SPLIT",FACE,{"disambiguationData":[TD([makeQuery(id+"F2.opExtrude","SWEPT_FACE",FACE,{"disambiguationData":[OSD([subQ5])]})])],"derivedFrom":makeQuery(id+"F3.boolean.opBoolean","COPY",FACE,{"derivedFrom":makeQuery(id+"F3.opExtrude","CAP_FACE",FACE,{"disambiguationData":[OSD([subQ5,subQ1,subQ6,subQ7,subQ4,subQ3,subQ2,subQ0])],"isStart":false})})}),makeQuery(id+"F8.opExtrude","SWEPT_FACE",FACE,{"disambiguationData":[OSD([sQuery(id+"F7.wireOp",EDGE,"E67")])]})]});}
            var Q5;
            Q5=makeQuery(id+"F8.boolean.opBoolean","INTERSECT",EDGE,{"disambiguationData":[OD(0.0)],"derivedFrom":[makeQuery(id+"F5.opExtrude","SWEPT_FACE",FACE,{"disambiguationData":[OSD([sQuery(id+"F4.wireOp",EDGE,"E30")])]}),makeQuery(id+"F8.opExtrude","SWEPT_FACE",FACE,{"disambiguationData":[OSD([sQuery(id+"F7.wireOp",EDGE,"E67")])]})]});
            fillet(context, id + "F14", {"entities" : qUnion([Q0, Q1, Q2, Q3, Q4, Q5]), "radius" : 3 * mm, "tangentPropagation" : true, "allowEdgeOverflow" : false});
        }
        {
            var Q0;
            Q0=makeQuery(id+"F1.opExtrude","CAP_EDGE",EDGE,{"disambiguationData":[OSD([sQuery(id+"F0.wireOp",EDGE,"E1.bottom")])],"isStart":false});
            fillet(context, id + "F15", {"entities" : qUnion([Q0]), "radius" : 2 * mm, "tangentPropagation" : true, "allowEdgeOverflow" : false});
        }
        {
            var Q0;
            {var subQ0=sQuery(id+"F0.wireOp",EDGE,"E22.filletArc");var subQ1=sQuery(id+"F0.wireOp",EDGE,"E7");var subQ2=sQuery(id+"F0.wireOp",EDGE,"E6");var subQ3=sQuery(id+"F0.wireOp",EDGE,"E5");var subQ4=sQuery(id+"F0.wireOp",EDGE,"E4");var subQ5=sQuery(id+"F0.wireOp",EDGE,"E1.bottom");var subQ6=sQuery(id+"F0.wireOp",EDGE,"E21.filletArc");var subQ7=sQuery(id+"F0.wireOp",EDGE,"E1.top");var subQ8=sQuery(id+"F0.wireOp",EDGE,"E1.left");var subQ9=sQuery(id+"F0.wireOp",EDGE,"E1.right");var subQ10=sQuery(id+"F0.wireOp",EDGE,"E23.filletArc");var subQ11=sQuery(id+"F0.wireOp",EDGE,"E24.filletArc");Q0=makeQuery(id+"F2.boolean.opBoolean","SPLIT",FACE,{"disambiguationData":[TD([makeQuery(id+"F1.opExtrude","SWEPT_FACE",FACE,{"disambiguationData":[OSD([subQ5])]})])],"derivedFrom":makeQuery(id+"F1.opExtrude","CAP_FACE",FACE,{"disambiguationData":[OSD([subQ5,subQ7,subQ8,subQ9,subQ4,subQ3,subQ2,subQ1,subQ6,subQ0,subQ10,subQ11])],"isStart":true})});}
            var sketch = newSketch(context, id + "F16", { "sketchPlane" : qUnion([Q0])});
            skSolve(sketch);
        }
        {
            var Q0;
            Q0=makeQuery(id+"F16.imprint","IMPRINT",FACE,{"disambiguationData":[TD([[makeQuery(id+"F16.imprint","IMPRINT",EDGE,{"derivedFrom":makeQuery(id+"F1.opExtrude","CAP_EDGE",EDGE,{"disambiguationData":[OSD([sQuery(id+"F0.wireOp",EDGE,"E1.bottom")])],"isStart":true})}),1.0]])]});
            var sketch = newSketch(context, id + "F17", { "sketchPlane" : qUnion([Q0])});
            skLineSegment(sketch, "E79.0.0", {"start": v(-80, 64.25) * mm, "end": v(-80, -64.25) * mm});
            skArc(sketch, "E79.0.1", {"start": v(-80, -64.25) * mm, "mid": v(-77.07, -71.32) * mm, "end": v(-70, -74.25) * mm});
            skLineSegment(sketch, "E79.0.2", {"start": v(-70, -74.25) * mm, "end": v(70, -74.25) * mm});
            skArc(sketch, "E79.0.3", {"start": v(70, -74.25) * mm, "mid": v(77.07, -71.32) * mm, "end": v(80, -64.25) * mm});
            skLineSegment(sketch, "E79.0.4", {"start": v(80, -64.25) * mm, "end": v(80, 64.25) * mm});
            skArc(sketch, "E79.0.5", {"start": v(80, 64.25) * mm, "mid": v(77.07, 71.32) * mm, "end": v(70, 74.25) * mm});
            skLineSegment(sketch, "E79.0.6", {"start": v(70, 74.25) * mm, "end": v(-70, 74.25) * mm});
            skArc(sketch, "E79.0.7", {"start": v(-70, 74.25) * mm, "mid": v(-77.07, 71.32) * mm, "end": v(-80, 64.25) * mm});
            skArc(sketch, "E80", {"start": v(15, 104.25) * mm, "mid": v(0, 119.25) * mm, "end": v(-15, 104.25) * mm});
            skPoint(sketch, "E80.centerSnap0", {"position": v(0, 74.25) * mm});
            skLineSegment(sketch, "E81", {"start": v(-15, 104.25) * mm, "end": v(-15, 92.25) * mm});
            skLineSegment(sketch, "E82", {"start": v(15, 104.25) * mm, "end": v(15, 92.25) * mm});
            skLineSegment(sketch, "E83", {"start": v(-15, 92.25) * mm, "end": v(-33, 74.25) * mm});
            skLineSegment(sketch, "E84", {"start": v(15, 92.25) * mm, "end": v(33, 74.25) * mm});
            skCircle(sketch, "E85", {"center": v(0, 104.25) * mm, "radius": 6 * mm});
            skLineSegment(sketch, "E86", {"start": v(0, 104.25) * mm, "end": v(0, 74.25) * mm, "construction": true});
            skLineSegment(sketch, "E87", {"start": v(-80, 0) * mm, "end": v(80, 0) * mm, "construction": true});
            skLineSegment(sketch, "E88.MirrorCS", {"start": v(15, -92.25) * mm, "end": v(33, -74.25) * mm});
            skPoint(sketch, "E89.MirrorP", {"position": v(0, -74.25) * mm});
            skLineSegment(sketch, "E90.MirrorCS", {"start": v(-15, -92.25) * mm, "end": v(-33, -74.25) * mm});
            skLineSegment(sketch, "E91.MirrorCS", {"start": v(0, -104.25) * mm, "end": v(0, -74.25) * mm, "construction": true});
            skLineSegment(sketch, "E92.MirrorCS", {"start": v(15, -104.25) * mm, "end": v(15, -92.25) * mm});
            skCircle(sketch, "E93.MirrorC", {"center": v(0, -104.25) * mm, "radius": 6 * mm});
            skArc(sketch, "E94.MirrorCS", {"start": v(15, -104.25) * mm, "mid": v(0, -119.25) * mm, "end": v(-15, -104.25) * mm});
            skLineSegment(sketch, "E95.MirrorCS", {"start": v(-15, -104.25) * mm, "end": v(-15, -92.25) * mm});
            skSolve(sketch);
        }
        {
            var Q0;
            {var subQ1=sQuery(id+"F17.wireOp",EDGE,"E88.MirrorCS");Q0=makeQuery(id+"F17.imprint","IMPRINT",FACE,{"disambiguationData":[TD([[makeQuery(id+"F17.imprint","IMPRINT",EDGE,{"derivedFrom":subQ1}),1.0]])]});}
            var Q1;
            Q1=makeQuery(id+"F17.imprint","IMPRINT",FACE,{"disambiguationData":[TD([[makeQuery(id+"F17.imprint","IMPRINT",EDGE,{"derivedFrom":sQuery(id+"F17.wireOp",EDGE,"E80")}),1.0]])]});
            var Q2;
            Q2=makeQuery(id+"F16.imprint","IMPRINT",FACE,{"disambiguationData":[TD([[makeQuery(id+"F16.imprint","IMPRINT",EDGE,{"derivedFrom":makeQuery(id+"F1.opExtrude","CAP_EDGE",EDGE,{"disambiguationData":[OSD([sQuery(id+"F0.wireOp",EDGE,"E1.bottom")])],"isStart":true})}),1.0]])]});
            var Q3;
            Q3=makeQuery(id+"F2.opExtrude","CAP_FACE",FACE,{"disambiguationData":[OSD([sQuery(id+"F0.wireOp",EDGE,"E12"),sQuery(id+"F0.wireOp",EDGE,"E13"),sQuery(id+"F0.wireOp",EDGE,"E14"),sQuery(id+"F0.wireOp",EDGE,"E15"),sQuery(id+"F0.wireOp",EDGE,"E17.filletArc"),sQuery(id+"F0.wireOp",EDGE,"E18.filletArc"),sQuery(id+"F0.wireOp",EDGE,"E19.filletArc"),sQuery(id+"F0.wireOp",EDGE,"E20.filletArc"),sQuery(id+"F0.wireOp",EDGE,"E25.0"),sQuery(id+"F0.wireOp",EDGE,"E25.1"),sQuery(id+"F0.wireOp",EDGE,"E25.2"),sQuery(id+"F0.wireOp",EDGE,"E25.3"),sQuery(id+"F0.wireOp",EDGE,"E25.4"),sQuery(id+"F0.wireOp",EDGE,"E25.5"),sQuery(id+"F0.wireOp",EDGE,"E25.6"),sQuery(id+"F0.wireOp",EDGE,"E25.7")])],"isStart":false});
            extrude(context, id + "F18", {"entities" : qUnion([Q0, Q1, Q2]), "endBound" : BoundingType.UP_TO_SURFACE, "endBoundEntityFace" : qUnion([Q3]), "depth" : 25 * mm});
        }
    });
